# Revit family: 0068074
name_source: partatom
category: Lighting Fixtures
revit_build: Autodesk Revit 2017 (Build: 20190507_1515(x64)
units: mm (PartAtom-declared; Revit-internal decimal feet)

## family parameters
Cut with Voids When Loaded = Yes
Host = Face
Light Source = Yes
OmniClass Number = 23.80.70.11.14
OmniClass Title = General Luminaries, Directional
Part Type = Normal
Room Calculation Point = No
Round Connector Dimension = Use Diameter
Shared = No

## types (1)
- 0068074 ST WTRPRF GRP T 1500 HO IP65 8300LM 840Q
    AccessoryMaterial = Diffuser-Sylvania-Glow
    Apparent Load = 67 VA
    Assembly Code = D5020200
    AssetType = Fixed
    BodyMaterial = Body-Sylvania-Gray
    ClassificationName = Uniclass2015
    ClassificationValue = EF_70_80
    Color Filter = 16777215
    Cost = 0 $
    Default Elevation = 1219 mm
    Description = Start Waterproof, integrated LED weatherproof luminaire, with UV stabilized flat diffuser and linear prisms designed to achieve uniform lit appearance, optimise light output and to reduce glare, stainless steel diffuser clips and fixing brackets for surface and wall mounting. Glass Reinforced Plastic housing for robustness, Polycarbonate diffuser, 8300lm, 67W, 124 lm/W, 4000 K, drive current 1010 mA, non dimmable, 3 hours emergency, CRI 80, IP65, IK08, Class I, nominal average life (h): 50000, 1578mm x 110mm x 78mm, energy class: A++ A+ A, D-mark
    DiffuserMaterial = Diffuser-Sylvania-Transparent
    Dimming Lamp Color Temperature Shift = <None>
    DocumentationLiterature = http://www.sylvania-lighting.com
    DurationUnit = hours
    ElectricShockClassification = Class I
    Emit Shape Visible in Rendering = No
    Emit from Rectangle Length = 1552 mm  [stored 5.09186 ft]
    Emit from Rectangle Width = 90 mm  [stored 0.295276 ft]
    ExpectedLife = 50000
    IfcExportAs = IfcLightFixtureType
    IfcExportType = IfcLightFixtureType
    ImpactProtectionIndex = IK08
    IngressProtection = IP65
    Keynote = 16500
    Lamp = LED
    LampColourRenderingIndex = 80
    LampColourTemperature = 4000 K
    LampMacAdamStep = 5
    LampNominalLuminous = 8300 lm
    LampsType = LED
    Length = 1572 mm  [stored 5.15748 ft]
    LuminousEfficacy = 124 lm/W
    Manufacturer = Feilo Sylvania
    ManufacturerName = Feilo Sylvania
    Material = composite material housing, pc polycarbonate diffuser
    Model = START Waterproof GRP Twin 1500 HO IP65 8300lm 840Q
    ModelNumber = 0068074
    ModelReference = START Waterproof GRP Twin 1500 HO IP65 8300lm 840Q
    Name = START Waterproof GRP Twin 1500 HO IP65 8300lm 840Q
    NominalHeight = 78 mm  [stored 0.255906 ft]
    NominalLength = 1578 mm  [stored 5.17717 ft]
    NominalWidth = 0 mm  [stored 0 ft]
    Photometric Web File = 0068074.ies
    PowerConsumption = 67 W
    PowerFactor = 0.99
    ReflectorMaterial = <By Category>
    Tilt Angle = -90.00°
    Type Image = <None>
    TypeName = START Waterproof GRP Twin 1500 HO IP65 8300lm 840Q
    URL = http://www.sylvania-lighting.com
    Voltage = 0 V
    Weight = 2.73 kg
    Width = 110 mm  [stored 0.360892 ft]

note: [stored X ft] marks values corroborated as IEEE doubles in the binary element streams (Revit-internal decimal feet)

## geometry (parser evidence)
native form markers: Sweep x5
no freeform markers — native parametric forms only
